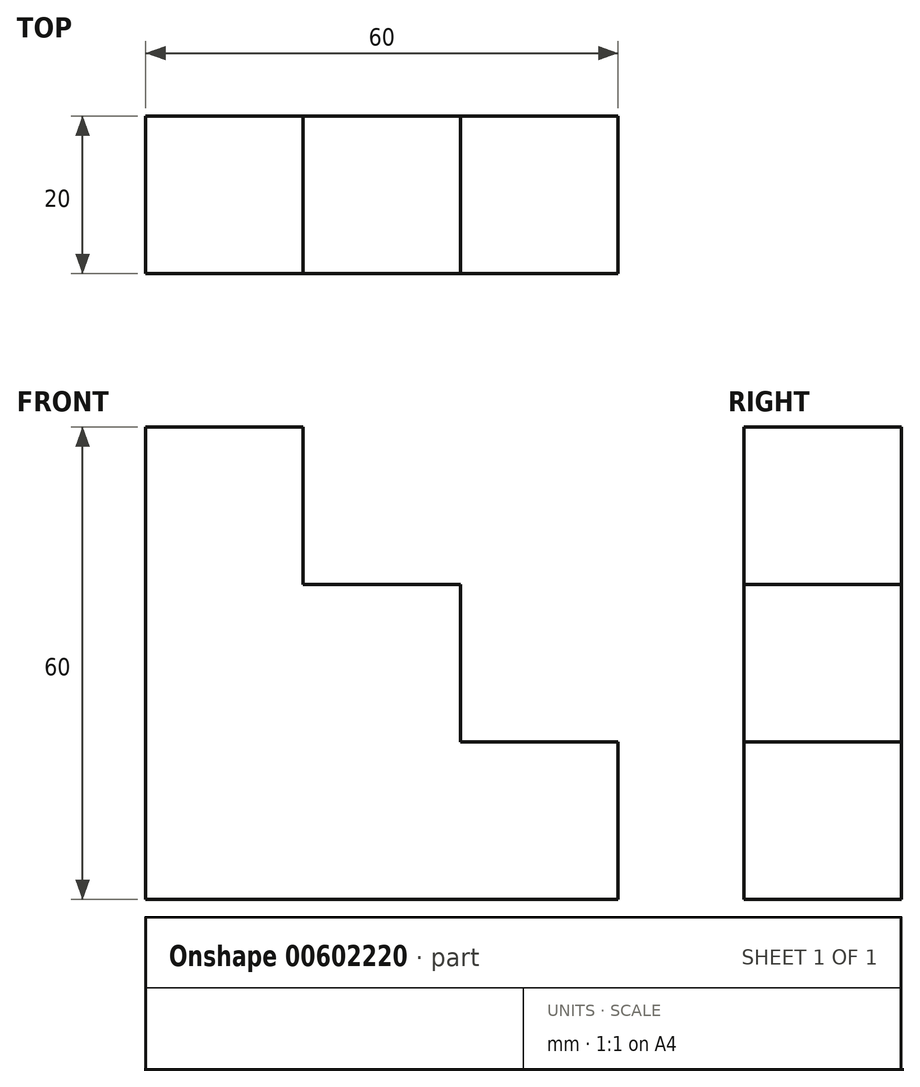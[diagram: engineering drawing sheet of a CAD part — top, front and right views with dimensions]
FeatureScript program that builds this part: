
annotation { "Feature Type Name" : "Feature", "Feature Type Description" : "" }
export const myFeature = defineFeature(function(context is Context, id is Id, definition is map)
    precondition{}
    {
        {
            var Q0;
            Q0=qCreatedBy(makeId("Front.planeOp"),FACE);
            var sketch = newSketch(context, id + "F0", { "sketchPlane" : qUnion([Q0])});
            skLineSegment(sketch, "E0", {"start": v(-67.04, -31.09) * mm, "end": v(-7.04, -31.09) * mm});
            skLineSegment(sketch, "E1", {"start": v(-7.04, -31.09) * mm, "end": v(-7.04, -11.09) * mm});
            skLineSegment(sketch, "E2", {"start": v(-7.04, -11.09) * mm, "end": v(-27.04, -11.09) * mm});
            skLineSegment(sketch, "E3", {"start": v(-27.04, -11.09) * mm, "end": v(-27.04, 8.91) * mm});
            skLineSegment(sketch, "E4", {"start": v(-27.04, 8.91) * mm, "end": v(-47.04, 8.91) * mm});
            skLineSegment(sketch, "E5", {"start": v(-47.04, 8.91) * mm, "end": v(-47.04, 28.91) * mm});
            skLineSegment(sketch, "E6", {"start": v(-47.04, 28.91) * mm, "end": v(-67.04, 28.91) * mm});
            skLineSegment(sketch, "E7", {"start": v(-67.04, 28.91) * mm, "end": v(-67.04, -31.09) * mm});
            skSolve(sketch);
        }
        {
            var Q0;
            Q0=makeQuery(id+"F0.imprint","IMPRINT",FACE,{"disambiguationData":[TD([[makeQuery(id+"F0.imprint","IMPRINT",EDGE,{"derivedFrom":sQuery(id+"F0.wireOp",EDGE,"E0")}),1.0]])]});
            extrude(context, id + "F1", {"entities" : qUnion([Q0]), "depth" : 20 * mm, "offsetDistance" : 25 * mm});
        }
    });
